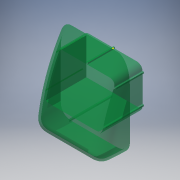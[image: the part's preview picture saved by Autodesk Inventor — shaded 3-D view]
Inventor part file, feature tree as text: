
AUTODESK INVENTOR PART (.ipt)
format: ipt  version: 2018 (Build 220112000, 112)  size: 488,448 bytes
history: native  units: in
note: dims shown in document units (in); Inventor stores cm internally (conversion verified against a paired STEP export)
features: sketch x8, extrude x6, fillet x2, shell x2, plane x1
ambient origin geometry x8: Origin, YZ Plane, XZ Plane, XY Plane, X Axis, Y Axis, Z Axis, Center Point
bodies: Solid1 (feature_tree)
feature tree (19):
  plane  "Work Plane1"
  extrude  "Extrusion1"  Depth=2.55in TaperAngle=0.0deg
  fillet  "Fillet1"  Radius=0.5in
  shell  "Shell1"  Thickness=0.07in
  sketch  "Sketch3"  dims[d3=-0.0175in d11=2.55in d12=0.0in d13=0.5in d14=0.07in]
  sketch  "Sketch4"  dims[d33=1.5in d36=0.0in d37=0.0in d38=0.1in d39=0.2in]
  sketch  "Sketch5"  dims[d40=0.05in d41=0.05in]
  extrude  "Extrusion4"  TaperAngle=0.0deg  [1 undecoded]
  shell  "Shell3"  Thickness=0.1in
  fillet  "Fillet3"  Radius=0.2in
  sketch  "Sketch6"  dims[d42=0.0in d43=0.0in d51=0.05in d52=0.05in d54=0.0in d55=0.0in]
  extrude  "Extrusion5"  Depth=0.05in
  extrude  "Extrusion8"  Depth=0.05in TaperAngle=0.0deg
  sketch  "Sketch7"  dims[d56=0.05in d57=90.0deg]
  sketch  "Sketch11"  dims[d60=0.05in]
  sketch  "Sketch10"  dims[d58=0.05in d59=90.0deg]
  sketch  "Sketch12"  dims[d63=1.0in d64=0.0in d67=0.05in d68=0.05in d69=0.05in d71=0.0in d72=1.0in d76=0.05in d77=90.0deg d78=0.05in d79=0.0in]
  extrude  "Extrusion7"  TaperAngle=90.0deg  [1 undecoded]
  extrude  "Extrusion9"  TaperAngle=90.0deg  [1 undecoded]
note: 3 required parameter values undecoded (feature->parameter linkage not recoverable at this tier; creation-order binding heuristic only, values carry confidence <= 0.55)
